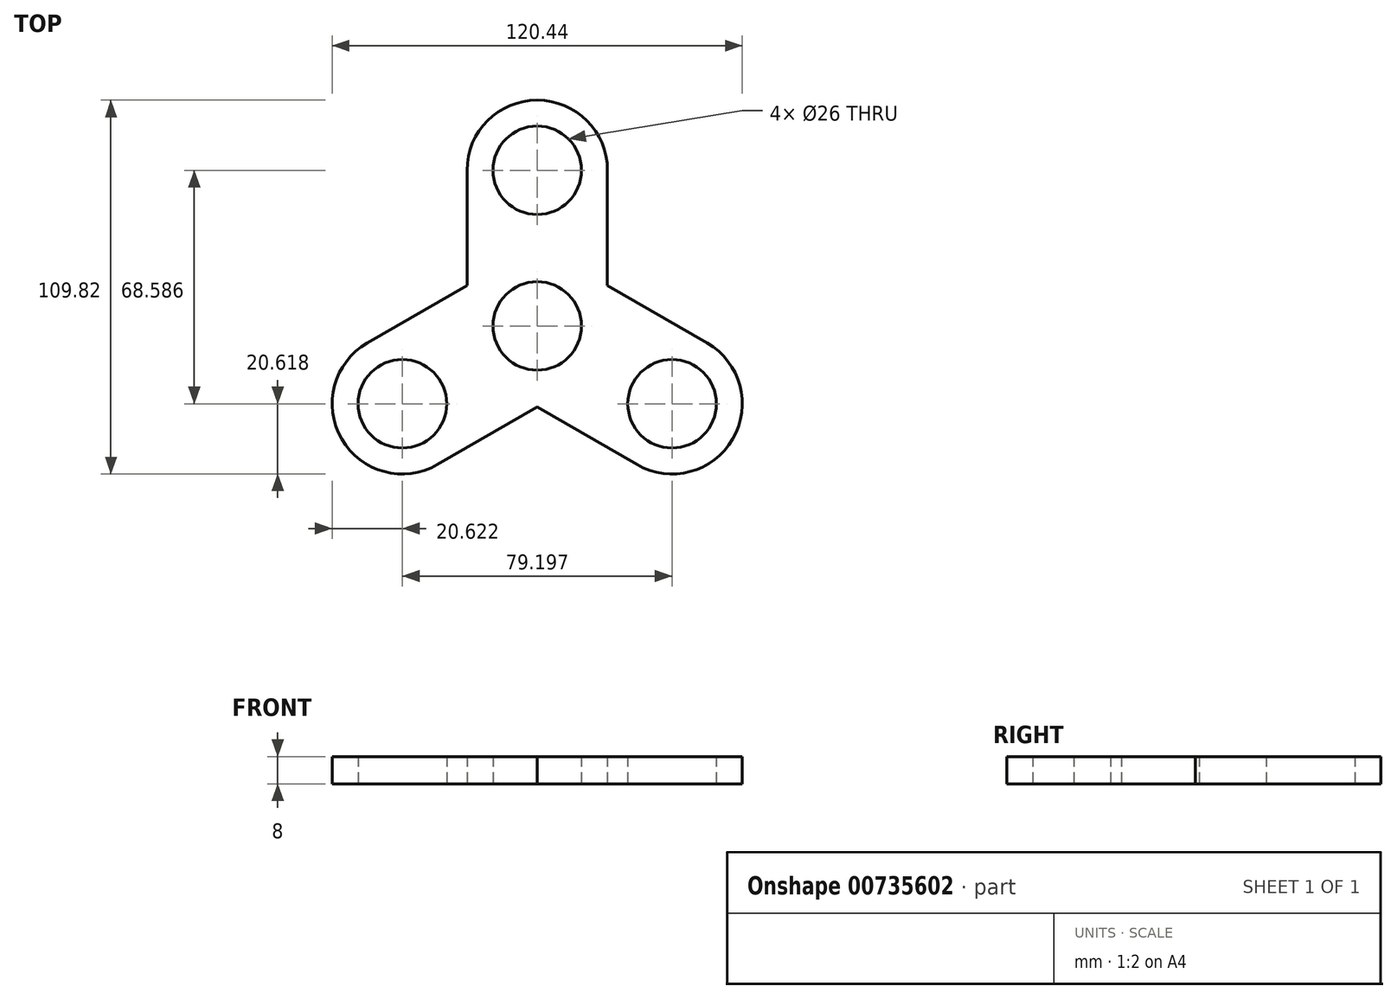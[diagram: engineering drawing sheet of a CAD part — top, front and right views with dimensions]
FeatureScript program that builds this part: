
annotation { "Feature Type Name" : "Feature", "Feature Type Description" : "" }
export const myFeature = defineFeature(function(context is Context, id is Id, definition is map)
    precondition{}
    {
        {
            var Q0;
            Q0=qCreatedBy(makeId("Top.planeOp"),FACE);
            var sketch = newSketch(context, id + "F0", { "sketchPlane" : qUnion([Q0])});
            skCircle(sketch, "E0", {"center": v(0, 0) * mm, "radius": 13 * mm});
            skCircle(sketch, "E1", {"center": v(0, 45.72) * mm, "radius": 13 * mm});
            skCircle(sketch, "E2.1.0", {"center": v(-39.6, -22.86) * mm, "radius": 13 * mm});
            skCircle(sketch, "E2.2.0", {"center": v(39.6, -22.86) * mm, "radius": 13 * mm});
            skCircle(sketch, "E3", {"center": v(0, 45.72) * mm, "radius": 20.62 * mm});
            skLineSegment(sketch, "E4", {"start": v(20.62, 45.72) * mm, "end": v(20.62, 11.9) * mm});
            skLineSegment(sketch, "E5", {"start": v(-20.62, 11.9) * mm, "end": v(-20.62, 45.72) * mm});
            skCircle(sketch, "E6", {"center": v(0, 0) * mm, "radius": 20.62 * mm});
            skCircle(sketch, "E7.1.0", {"center": v(-39.6, -22.86) * mm, "radius": 20.62 * mm});
            skCircle(sketch, "E7.2.0", {"center": v(39.6, -22.86) * mm, "radius": 20.62 * mm});
            skLineSegment(sketch, "E8.1.0", {"start": v(0, -23.8) * mm, "end": v(-29.29, -40.72) * mm});
            skLineSegment(sketch, "E8.1.1", {"start": v(-49.9, -5) * mm, "end": v(-20.62, 11.9) * mm});
            skLineSegment(sketch, "E8.2.0", {"start": v(20.62, 11.9) * mm, "end": v(49.9, -5) * mm});
            skLineSegment(sketch, "E8.2.1", {"start": v(29.29, -40.72) * mm, "end": v(0, -23.8) * mm});
            skPoint(sketch, "E9.orphan", {"position": v(-10.3, 17.86) * mm});
            skPoint(sketch, "E10.orphan", {"position": v(-20.62, 0) * mm});
            skPoint(sketch, "E11.orphan", {"position": v(20.62, 0) * mm});
            skPoint(sketch, "E12.orphan", {"position": v(10.31, 17.86) * mm});
            skPoint(sketch, "E13.orphan", {"position": v(10.3, -17.86) * mm});
            skPoint(sketch, "E14.orphan", {"position": v(-10.31, -17.86) * mm});
            skSolve(sketch);
        }
        {
            var Q0;
            {var subQ1=sQuery(id+"F0.wireOp",EDGE,"E4");Q0=makeQuery(id+"F0.imprint","IMPRINT",FACE,{"disambiguationData":[TD([[makeQuery(id+"F0.imprint","IMPRINT",EDGE,{"derivedFrom":subQ1}),-1.0]])]});}
            var Q1;
            Q1=makeQuery(id+"F0.imprint","IMPRINT",FACE,{"disambiguationData":[TD([[makeQuery(id+"F0.imprint","IMPRINT",EDGE,{"derivedFrom":sQuery(id+"F0.wireOp",EDGE,"E1")}),-1.0]])]});
            var Q2;
            Q2=makeQuery(id+"F0.imprint","IMPRINT",FACE,{"disambiguationData":[TD([[makeQuery(id+"F0.imprint","IMPRINT",EDGE,{"derivedFrom":sQuery(id+"F0.wireOp",EDGE,"E2.2.0")}),-1.0]])]});
            var Q3;
            Q3=makeQuery(id+"F0.imprint","IMPRINT",FACE,{"disambiguationData":[TD([[makeQuery(id+"F0.imprint","IMPRINT",EDGE,{"derivedFrom":sQuery(id+"F0.wireOp",EDGE,"E0")}),-1.0]])]});
            var Q4;
            Q4=makeQuery(id+"F0.imprint","IMPRINT",FACE,{"disambiguationData":[TD([[makeQuery(id+"F0.imprint","IMPRINT",EDGE,{"derivedFrom":sQuery(id+"F0.wireOp",EDGE,"E2.1.0")}),-1.0]])]});
            extrude(context, id + "F1", {"entities" : qUnion([Q0, Q1, Q2, Q3, Q4]), "endBound" : BoundingType.SYMMETRIC, "depth" : 8 * mm, "offsetDistance" : 25.4 * mm});
        }
    });
